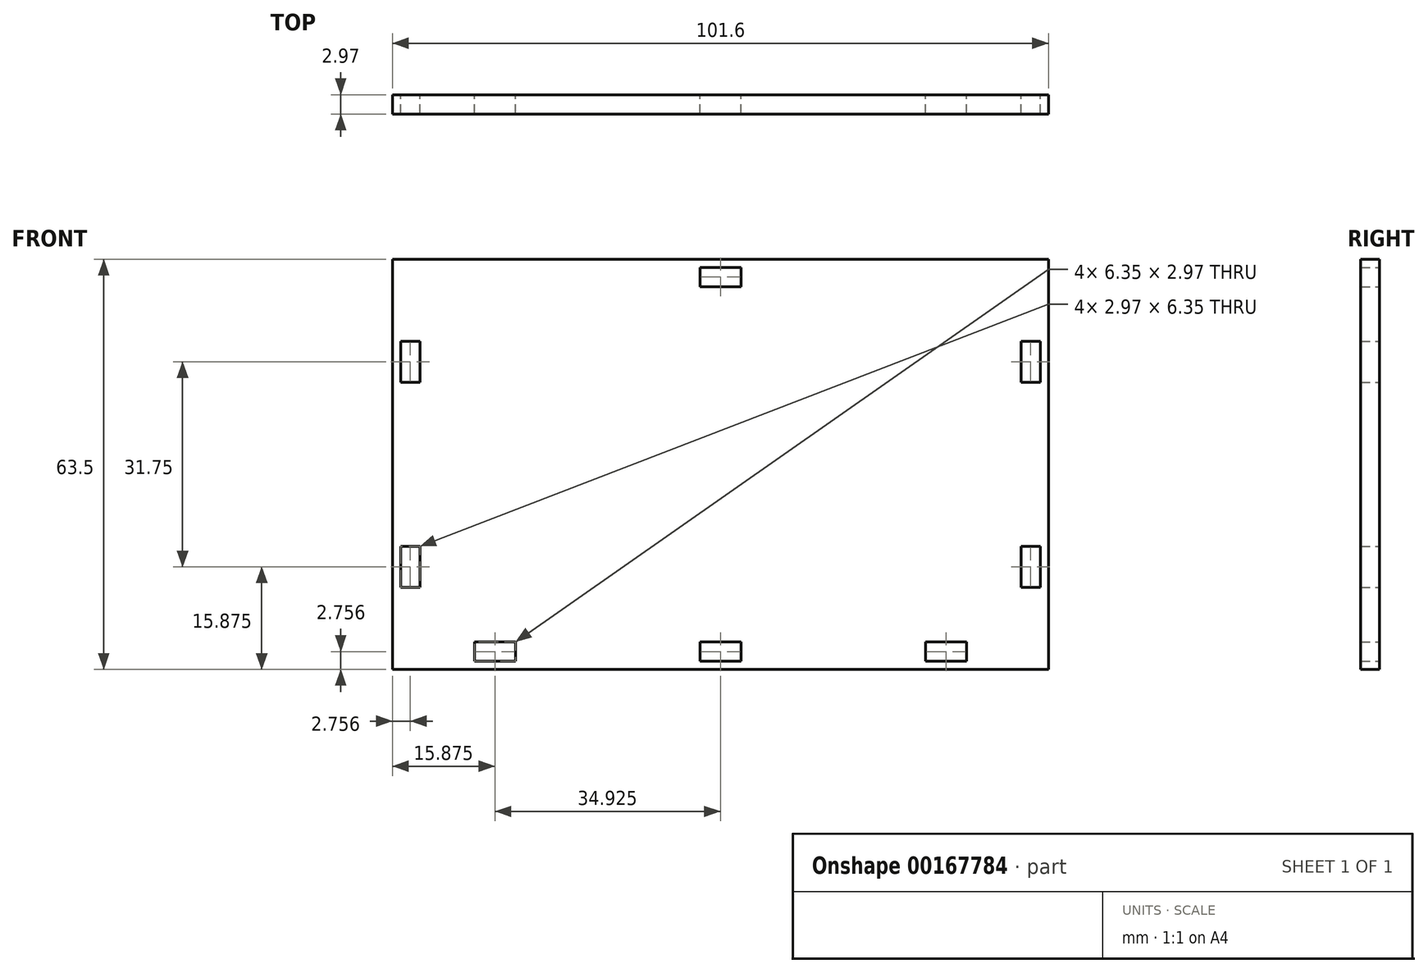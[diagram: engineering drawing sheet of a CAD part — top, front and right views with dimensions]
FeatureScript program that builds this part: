
annotation { "Feature Type Name" : "Feature", "Feature Type Description" : "" }
export const myFeature = defineFeature(function(context is Context, id is Id, definition is map)
    precondition{}
    {
        {
            var Q0;
            Q0=qCreatedBy(makeId("Front.planeOp"),FACE);
            var sketch = newSketch(context, id + "F0", { "sketchPlane" : qUnion([Q0])});
            skLineSegment(sketch, "E0.bottom", {"start": v(50.8, 31.75) * mm, "end": v(-50.8, 31.75) * mm});
            skLineSegment(sketch, "E0.top", {"start": v(50.8, -31.75) * mm, "end": v(-50.8, -31.75) * mm});
            skLineSegment(sketch, "E0.left", {"start": v(50.8, 31.75) * mm, "end": v(50.8, -31.75) * mm});
            skLineSegment(sketch, "E0.right", {"start": v(-50.8, 31.75) * mm, "end": v(-50.8, -31.75) * mm});
            skPoint(sketch, "E0.middle", {"position": v(0, 0) * mm});
            skLineSegment(sketch, "E1.bottom", {"start": v(-38.1, -27.5) * mm, "end": v(-31.75, -27.5) * mm});
            skLineSegment(sketch, "E1.top", {"start": v(-38.1, -30.48) * mm, "end": v(-31.75, -30.48) * mm});
            skLineSegment(sketch, "E1.left", {"start": v(-38.1, -27.5) * mm, "end": v(-38.1, -30.48) * mm});
            skLineSegment(sketch, "E1.right", {"start": v(-31.75, -27.5) * mm, "end": v(-31.75, -30.48) * mm});
            skLineSegment(sketch, "E2", {"start": v(0, 31.75) * mm, "end": v(0, -31.75) * mm, "construction": true});
            skLineSegment(sketch, "E3", {"start": v(-50.8, 0) * mm, "end": v(50.8, 0) * mm, "construction": true});
            skLineSegment(sketch, "E4.MirrorCS", {"start": v(38.1, -27.5) * mm, "end": v(31.75, -27.5) * mm});
            skLineSegment(sketch, "E5.MirrorCS", {"start": v(38.1, -30.48) * mm, "end": v(31.75, -30.48) * mm});
            skLineSegment(sketch, "E6.MirrorCS", {"start": v(31.75, -27.5) * mm, "end": v(31.75, -30.48) * mm});
            skLineSegment(sketch, "E7.MirrorCS", {"start": v(38.1, -27.5) * mm, "end": v(38.1, -30.48) * mm});
            skLineSegment(sketch, "E8.bottom", {"start": v(-3.18, -27.5) * mm, "end": v(3.17, -27.5) * mm});
            skLineSegment(sketch, "E8.top", {"start": v(-3.18, -30.48) * mm, "end": v(3.17, -30.48) * mm});
            skLineSegment(sketch, "E8.left", {"start": v(-3.18, -27.5) * mm, "end": v(-3.18, -30.48) * mm});
            skLineSegment(sketch, "E8.right", {"start": v(3.17, -27.5) * mm, "end": v(3.17, -30.48) * mm});
            skLineSegment(sketch, "E9.bottom", {"start": v(-49.53, 19.05) * mm, "end": v(-46.56, 19.05) * mm});
            skLineSegment(sketch, "E9.top", {"start": v(-49.53, 12.7) * mm, "end": v(-46.56, 12.7) * mm});
            skLineSegment(sketch, "E9.left", {"start": v(-49.53, 19.05) * mm, "end": v(-49.53, 12.7) * mm});
            skLineSegment(sketch, "E9.right", {"start": v(-46.56, 19.05) * mm, "end": v(-46.56, 12.7) * mm});
            skLineSegment(sketch, "E10.MirrorCS", {"start": v(-49.53, -19.05) * mm, "end": v(-49.53, -12.7) * mm});
            skLineSegment(sketch, "E11.MirrorCS", {"start": v(-46.56, -19.05) * mm, "end": v(-46.56, -12.7) * mm});
            skLineSegment(sketch, "E12.MirrorCS", {"start": v(-49.53, -12.7) * mm, "end": v(-46.56, -12.7) * mm});
            skLineSegment(sketch, "E13.MirrorCS", {"start": v(-49.53, -19.05) * mm, "end": v(-46.56, -19.05) * mm});
            skLineSegment(sketch, "E14.MirrorCS", {"start": v(49.53, 19.05) * mm, "end": v(46.56, 19.05) * mm});
            skLineSegment(sketch, "E15.MirrorCS", {"start": v(49.53, 19.05) * mm, "end": v(49.53, 12.7) * mm});
            skLineSegment(sketch, "E16.MirrorCS", {"start": v(46.56, 19.05) * mm, "end": v(46.56, 12.7) * mm});
            skLineSegment(sketch, "E17.MirrorCS", {"start": v(49.53, 12.7) * mm, "end": v(46.56, 12.7) * mm});
            skLineSegment(sketch, "E18.MirrorCS", {"start": v(49.53, -12.7) * mm, "end": v(46.56, -12.7) * mm});
            skLineSegment(sketch, "E19.MirrorCS", {"start": v(49.53, -19.05) * mm, "end": v(49.53, -12.7) * mm});
            skLineSegment(sketch, "E20.MirrorCS", {"start": v(49.53, -19.05) * mm, "end": v(46.56, -19.05) * mm});
            skLineSegment(sketch, "E21.MirrorCS", {"start": v(46.56, -19.05) * mm, "end": v(46.56, -12.7) * mm});
            skLineSegment(sketch, "E22.bottom", {"start": v(3.17, 27.5) * mm, "end": v(-3.18, 27.5) * mm});
            skLineSegment(sketch, "E22.top", {"start": v(3.17, 30.48) * mm, "end": v(-3.18, 30.48) * mm});
            skLineSegment(sketch, "E22.left", {"start": v(3.17, 27.5) * mm, "end": v(3.17, 30.48) * mm});
            skLineSegment(sketch, "E22.right", {"start": v(-3.18, 27.5) * mm, "end": v(-3.18, 30.48) * mm});
            skPoint(sketch, "E22.middle", {"position": v(0, 29) * mm});
            skSolve(sketch);
        }
        {
            var Q0;
            Q0 = qSketchRegion(id + "F0", true);
            extrude(context, id + "F1", {"entities" : qUnion([Q0]), "depth" : 2.97 * mm});
        }
    });
